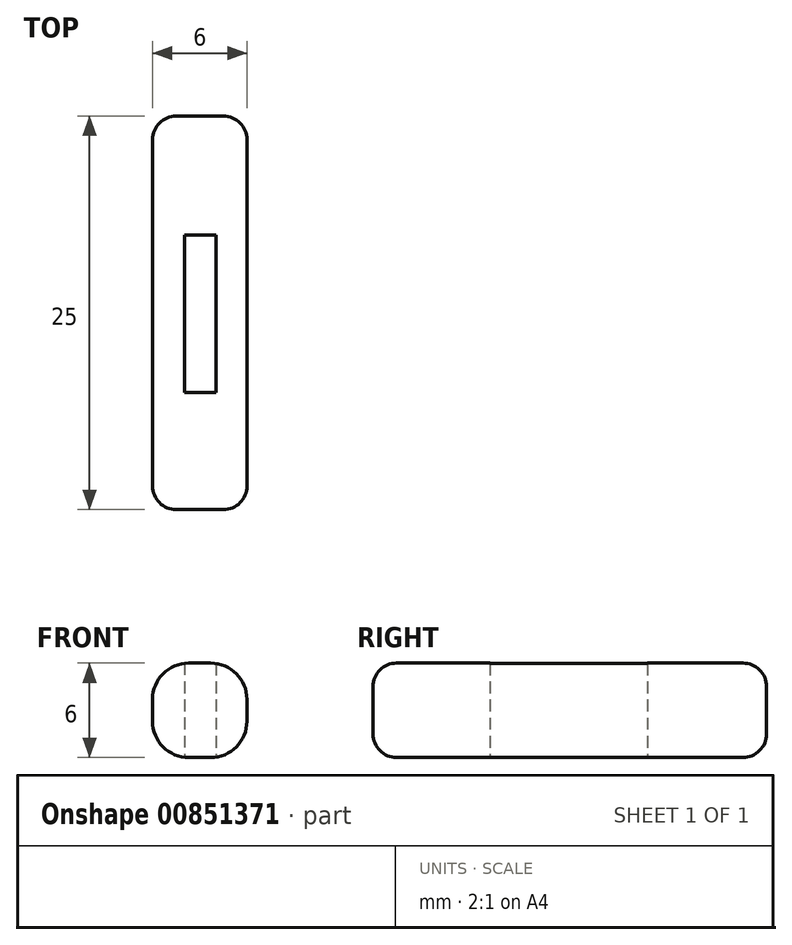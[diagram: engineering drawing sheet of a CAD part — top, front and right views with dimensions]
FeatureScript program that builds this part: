
annotation { "Feature Type Name" : "Feature", "Feature Type Description" : "" }
export const myFeature = defineFeature(function(context is Context, id is Id, definition is map)
    precondition{}
    {
        {
            var Q0;
            Q0=qCreatedBy(makeId("Top.planeOp"),FACE);
            var sketch = newSketch(context, id + "F0", { "sketchPlane" : qUnion([Q0])});
            skLineSegment(sketch, "E0.bottom", {"start": v(-13.77, 10.4) * mm, "end": v(-7.77, 10.4) * mm});
            skLineSegment(sketch, "E0.top", {"start": v(-13.77, -14.6) * mm, "end": v(-7.77, -14.6) * mm});
            skLineSegment(sketch, "E0.left", {"start": v(-13.77, 10.4) * mm, "end": v(-13.77, -14.6) * mm});
            skLineSegment(sketch, "E0.right", {"start": v(-7.77, 10.4) * mm, "end": v(-7.77, -14.6) * mm});
            skLineSegment(sketch, "E1.bottom", {"start": v(-11.75, 2.83) * mm, "end": v(-9.75, 2.83) * mm});
            skLineSegment(sketch, "E1.top", {"start": v(-11.75, -7.17) * mm, "end": v(-9.75, -7.17) * mm});
            skLineSegment(sketch, "E1.left", {"start": v(-11.75, 2.83) * mm, "end": v(-11.75, -7.17) * mm});
            skLineSegment(sketch, "E1.right", {"start": v(-9.75, 2.83) * mm, "end": v(-9.75, -7.17) * mm});
            skSolve(sketch);
        }
        {
            var Q0;
            Q0=makeQuery(id+"F0.imprint","IMPRINT",FACE,{"disambiguationData":[TD([[makeQuery(id+"F0.imprint","IMPRINT",EDGE,{"derivedFrom":sQuery(id+"F0.wireOp",EDGE,"E0.bottom")}),-1.0]])]});
            extrude(context, id + "F1", {"entities" : qUnion([Q0]), "depth" : 6 * mm, "offsetDistance" : 25 * mm});
        }
        {
            var Q0;
            Q0=makeQuery(id+"F1.opExtrude","CAP_EDGE",EDGE,{"disambiguationData":[OSD([sQuery(id+"F0.wireOp",EDGE,"E0.left")])],"isStart":false});
            var Q1;
            Q1=makeQuery(id+"F1.opExtrude","CAP_EDGE",EDGE,{"disambiguationData":[OSD([sQuery(id+"F0.wireOp",EDGE,"E0.left")])],"isStart":true});
            var Q2;
            Q2=makeQuery(id+"F1.opExtrude","CAP_EDGE",EDGE,{"disambiguationData":[OSD([sQuery(id+"F0.wireOp",EDGE,"E0.right")])],"isStart":false});
            var Q3;
            Q3=makeQuery(id+"F1.opExtrude","CAP_EDGE",EDGE,{"disambiguationData":[OSD([sQuery(id+"F0.wireOp",EDGE,"E0.right")])],"isStart":true});
            fillet(context, id + "F2", {"entities" : qUnion([Q0, Q1, Q2, Q3]), "radius" : 2.3 * mm, "tangentPropagation" : true, "allowEdgeOverflow" : false});
        }
        {
            var Q0;
            Q0=makeQuery(id+"F2.opFillet","BLEND_EDGE",EDGE,{"blendedFrom":[makeQuery(id+"F1.opExtrude","CAP_EDGE",EDGE,{"disambiguationData":[OSD([sQuery(id+"F0.wireOp",EDGE,"E0.right")])],"isStart":false}),makeQuery(id+"F1.opExtrude","SWEPT_FACE",FACE,{"disambiguationData":[OSD([sQuery(id+"F0.wireOp",EDGE,"E0.bottom")])]})],"blendedInto":[makeQuery(id+"F1.opExtrude","SWEPT_FACE",FACE,{"disambiguationData":[OSD([sQuery(id+"F0.wireOp",EDGE,"E0.bottom")])]})]});
            var Q1;
            Q1=makeQuery(id+"F1.opExtrude","CAP_EDGE",EDGE,{"disambiguationData":[OSD([sQuery(id+"F0.wireOp",EDGE,"E0.bottom")])],"isStart":false});
            var Q2;
            Q2=makeQuery(id+"F2.opFillet","BLEND_EDGE",EDGE,{"blendedFrom":[makeQuery(id+"F1.opExtrude","CAP_EDGE",EDGE,{"disambiguationData":[OSD([sQuery(id+"F0.wireOp",EDGE,"E0.left")])],"isStart":false}),makeQuery(id+"F1.opExtrude","SWEPT_FACE",FACE,{"disambiguationData":[OSD([sQuery(id+"F0.wireOp",EDGE,"E0.bottom")])]})],"blendedInto":[makeQuery(id+"F1.opExtrude","SWEPT_FACE",FACE,{"disambiguationData":[OSD([sQuery(id+"F0.wireOp",EDGE,"E0.bottom")])]})]});
            var Q3;
            Q3=makeQuery(id+"F1.opExtrude","SWEPT_EDGE",EDGE,{"disambiguationData":[OSD([sQuery(id+"F0.wireOp",EDGE,"E0.bottom"),sQuery(id+"F0.wireOp",EDGE,"E0.left")])]});
            var Q4;
            Q4=makeQuery(id+"F2.opFillet","BLEND_EDGE",EDGE,{"blendedFrom":[makeQuery(id+"F1.opExtrude","CAP_EDGE",EDGE,{"disambiguationData":[OSD([sQuery(id+"F0.wireOp",EDGE,"E0.left")])],"isStart":true}),makeQuery(id+"F1.opExtrude","SWEPT_FACE",FACE,{"disambiguationData":[OSD([sQuery(id+"F0.wireOp",EDGE,"E0.bottom")])]})],"blendedInto":[makeQuery(id+"F1.opExtrude","SWEPT_FACE",FACE,{"disambiguationData":[OSD([sQuery(id+"F0.wireOp",EDGE,"E0.bottom")])]})]});
            var Q5;
            Q5=makeQuery(id+"F2.opFillet","BLEND_EDGE",EDGE,{"blendedFrom":[makeQuery(id+"F1.opExtrude","CAP_EDGE",EDGE,{"disambiguationData":[OSD([sQuery(id+"F0.wireOp",EDGE,"E0.right")])],"isStart":true}),makeQuery(id+"F1.opExtrude","SWEPT_FACE",FACE,{"disambiguationData":[OSD([sQuery(id+"F0.wireOp",EDGE,"E0.bottom")])]})],"blendedInto":[makeQuery(id+"F1.opExtrude","SWEPT_FACE",FACE,{"disambiguationData":[OSD([sQuery(id+"F0.wireOp",EDGE,"E0.bottom")])]})]});
            var Q6;
            Q6=makeQuery(id+"F1.opExtrude","SWEPT_EDGE",EDGE,{"disambiguationData":[OSD([sQuery(id+"F0.wireOp",EDGE,"E0.bottom"),sQuery(id+"F0.wireOp",EDGE,"E0.right")])]});
            var Q7;
            Q7=makeQuery(id+"F1.opExtrude","CAP_EDGE",EDGE,{"disambiguationData":[OSD([sQuery(id+"F0.wireOp",EDGE,"E0.bottom")])],"isStart":true});
            var Q8;
            Q8=makeQuery(id+"F2.opFillet","BLEND_EDGE",EDGE,{"blendedFrom":[makeQuery(id+"F1.opExtrude","CAP_EDGE",EDGE,{"disambiguationData":[OSD([sQuery(id+"F0.wireOp",EDGE,"E0.left")])],"isStart":true}),makeQuery(id+"F1.opExtrude","SWEPT_FACE",FACE,{"disambiguationData":[OSD([sQuery(id+"F0.wireOp",EDGE,"E0.top")])]})],"blendedInto":[makeQuery(id+"F1.opExtrude","SWEPT_FACE",FACE,{"disambiguationData":[OSD([sQuery(id+"F0.wireOp",EDGE,"E0.top")])]})]});
            fillet(context, id + "F3", {"entities" : qUnion([Q0, Q1, Q2, Q3, Q4, Q5, Q6, Q7, Q8]), "radius" : 1.5 * mm, "tangentPropagation" : true, "allowEdgeOverflow" : false});
        }
    });
